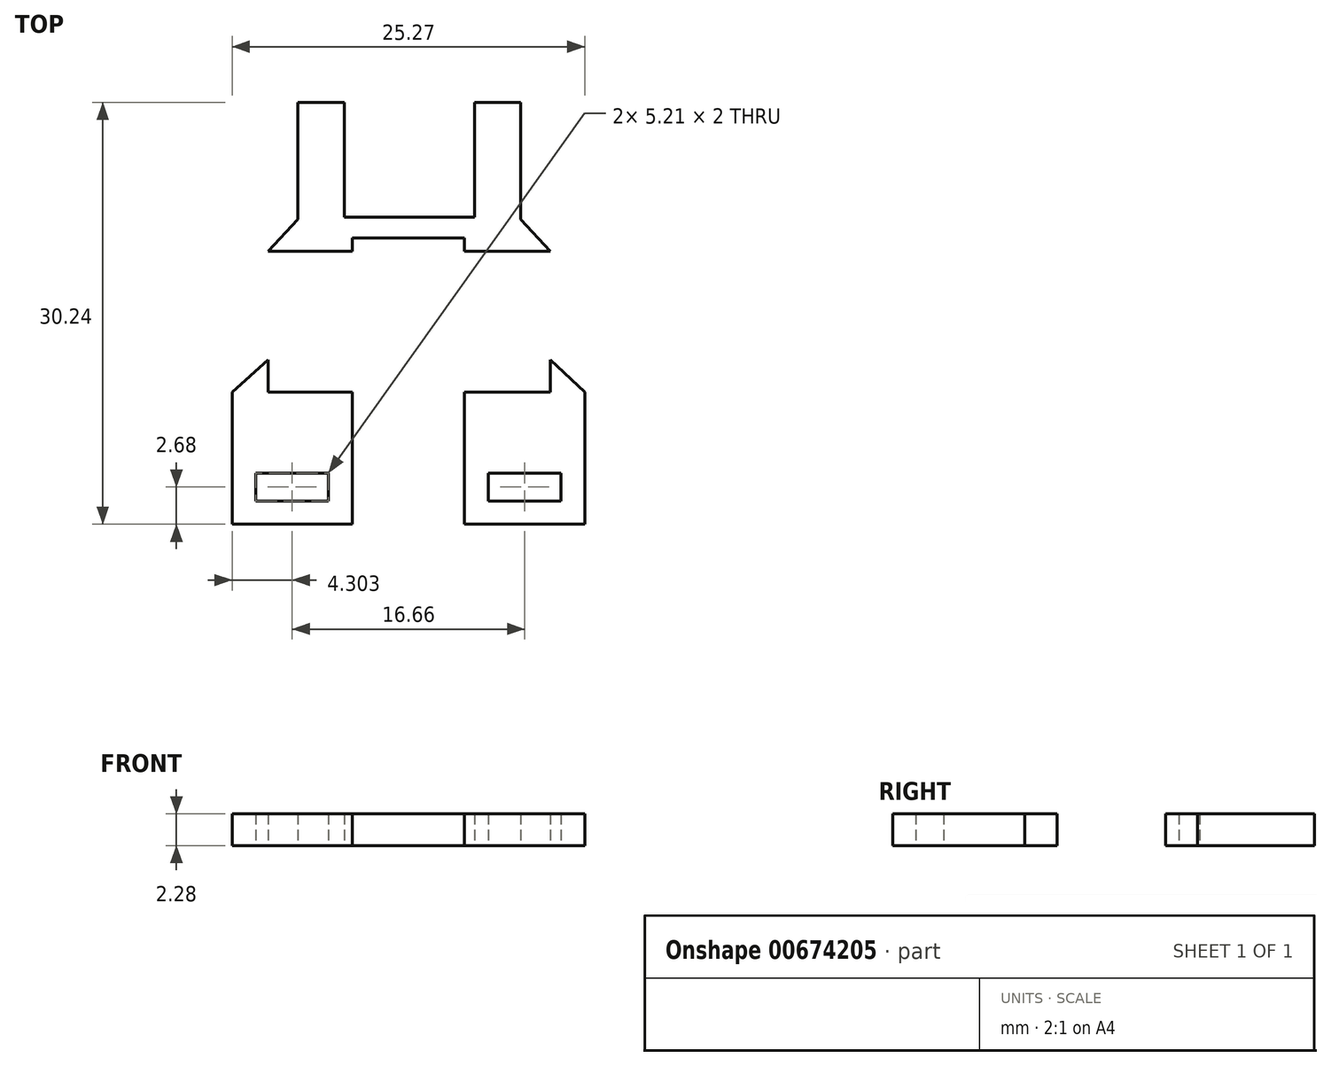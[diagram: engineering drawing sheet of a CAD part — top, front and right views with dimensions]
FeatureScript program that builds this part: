
annotation { "Feature Type Name" : "Feature", "Feature Type Description" : "" }
export const myFeature = defineFeature(function(context is Context, id is Id, definition is map)
    precondition{}
    {
        {
            var Q0;
            Q0=qCreatedBy(makeId("Top.planeOp"),FACE);
            var sketch = newSketch(context, id + "F0", { "sketchPlane" : qUnion([Q0])});
            skLineSegment(sketch, "E0.bottom", {"start": v(-2.7, 0) * mm, "end": v(6.6, 0) * mm});
            skLineSegment(sketch, "E0.top", {"start": v(-2.7, 8.22) * mm, "end": v(6.6, 8.22) * mm});
            skLineSegment(sketch, "E0.left", {"start": v(-2.7, 0) * mm, "end": v(-2.7, 8.22) * mm});
            skLineSegment(sketch, "E0.right", {"start": v(6.6, 0) * mm, "end": v(6.6, 8.22) * mm});
            skLineSegment(sketch, "E1.bottom", {"start": v(-6.03, 8.22) * mm, "end": v(9.94, 8.22) * mm});
            skLineSegment(sketch, "E1.top", {"start": v(-6.03, -2.45) * mm, "end": v(9.94, -2.45) * mm});
            skLineSegment(sketch, "E1.left", {"start": v(-6.03, 8.22) * mm, "end": v(-6.03, -2.45) * mm});
            skLineSegment(sketch, "E1.right", {"start": v(9.94, 8.22) * mm, "end": v(9.94, -2.45) * mm});
            skLineSegment(sketch, "E2.bottom", {"start": v(-8.19, -2.45) * mm, "end": v(12.05, -2.45) * mm});
            skLineSegment(sketch, "E2.top", {"start": v(-8.19, -12.54) * mm, "end": v(12.05, -12.54) * mm});
            skLineSegment(sketch, "E2.left", {"start": v(-8.19, -2.45) * mm, "end": v(-8.19, -12.54) * mm});
            skLineSegment(sketch, "E2.right", {"start": v(12.05, -2.45) * mm, "end": v(12.05, -12.54) * mm});
            skLineSegment(sketch, "E3.bottom", {"start": v(-10.75, -12.54) * mm, "end": v(14.52, -12.54) * mm});
            skLineSegment(sketch, "E3.top", {"start": v(-10.75, -22.02) * mm, "end": v(14.52, -22.02) * mm});
            skLineSegment(sketch, "E3.left", {"start": v(-10.75, -12.54) * mm, "end": v(-10.75, -22.02) * mm});
            skLineSegment(sketch, "E3.right", {"start": v(14.52, -12.54) * mm, "end": v(14.52, -22.02) * mm});
            skLineSegment(sketch, "E4.bottom", {"start": v(-2.14, -22.02) * mm, "end": v(5.9, -22.02) * mm});
            skLineSegment(sketch, "E4.top", {"start": v(-2.14, -1.51) * mm, "end": v(5.9, -1.51) * mm});
            skLineSegment(sketch, "E4.left", {"start": v(-2.14, -22.02) * mm, "end": v(-2.14, -1.51) * mm});
            skLineSegment(sketch, "E4.right", {"start": v(5.9, -22.02) * mm, "end": v(5.9, -1.5) * mm});
            skLineSegment(sketch, "E5", {"start": v(-10.75, -12.54) * mm, "end": v(-8.19, -10.24) * mm});
            skLineSegment(sketch, "E6", {"start": v(-8.19, -2.45) * mm, "end": v(-6.03, -0.15) * mm});
            skLineSegment(sketch, "E7", {"start": v(12.05, -2.45) * mm, "end": v(9.94, -0.15) * mm});
            skLineSegment(sketch, "E8", {"start": v(14.52, -12.54) * mm, "end": v(12.05, -10.24) * mm});
            skLineSegment(sketch, "E9.bottom", {"start": v(-9.05, -18.34) * mm, "end": v(-3.84, -18.34) * mm});
            skLineSegment(sketch, "E9.top", {"start": v(-9.05, -20.34) * mm, "end": v(-3.84, -20.34) * mm});
            skLineSegment(sketch, "E9.left", {"start": v(-9.05, -18.34) * mm, "end": v(-9.05, -20.34) * mm});
            skLineSegment(sketch, "E9.right", {"start": v(-3.84, -18.34) * mm, "end": v(-3.84, -20.34) * mm});
            skLineSegment(sketch, "E10.bottom", {"start": v(7.6, -18.34) * mm, "end": v(12.82, -18.34) * mm});
            skLineSegment(sketch, "E10.top", {"start": v(7.6, -20.34) * mm, "end": v(12.82, -20.34) * mm});
            skLineSegment(sketch, "E10.left", {"start": v(7.6, -18.34) * mm, "end": v(7.6, -20.34) * mm});
            skLineSegment(sketch, "E10.right", {"start": v(12.82, -18.34) * mm, "end": v(12.82, -20.34) * mm});
            skSolve(sketch);
        }
        {
            var Q0;
            {var subQ0=sQuery(id+"F0.wireOp",EDGE,"E3.right");Q0=makeQuery(id+"F0.imprint","IMPRINT",FACE,{"disambiguationData":[TD([[makeQuery(id+"F0.imprint","IMPRINT",EDGE,{"derivedFrom":subQ0}),-1.0]])]});}
            var Q1;
            {var subQ0=sQuery(id+"F0.wireOp",EDGE,"E3.left");Q1=makeQuery(id+"F0.imprint","IMPRINT",FACE,{"disambiguationData":[TD([[makeQuery(id+"F0.imprint","IMPRINT",EDGE,{"derivedFrom":subQ0}),1.0]])]});}
            var Q2;
            {var subQ3=sQuery(id+"F0.wireOp",EDGE,"E5");Q2=makeQuery(id+"F0.imprint","IMPRINT",FACE,{"disambiguationData":[TD([[makeQuery(id+"F0.imprint","IMPRINT",EDGE,{"derivedFrom":subQ3}),-1.0]])]});}
            var Q3;
            {var subQ4=sQuery(id+"F0.wireOp",EDGE,"E2.bottom");var subQ5=makeQuery(id+"F0.imprint","INTERSECT",VERTEX,{"derivedFrom":[sQuery(id+"F0.wireOp",EDGE,"E1.left"),subQ4]});Q3=makeQuery(id+"F0.imprint","IMPRINT",FACE,{"disambiguationData":[TD([[makeQuery(id+"F0.imprint","IMPRINT",EDGE,{"disambiguationData":[TD([[subQ5,-1.0]])],"derivedFrom":subQ4}),-1.0]])]});}
            var Q4;
            {var subQ3=sQuery(id+"F0.wireOp",EDGE,"E6");Q4=makeQuery(id+"F0.imprint","IMPRINT",FACE,{"disambiguationData":[TD([[makeQuery(id+"F0.imprint","IMPRINT",EDGE,{"derivedFrom":subQ3}),-1.0]])]});}
            var Q5;
            Q5=makeQuery(id+"F0.imprint","IMPRINT",FACE,{"disambiguationData":[TD([[makeQuery(id+"F0.imprint","IMPRINT",EDGE,{"derivedFrom":sQuery(id+"F0.wireOp",EDGE,"E0.bottom")}),-1.0]])]});
            var Q6;
            {var subQ1=sQuery(id+"F0.wireOp",EDGE,"E2.bottom");var subQ4=makeQuery(id+"F0.imprint","INTERSECT",VERTEX,{"derivedFrom":[sQuery(id+"F0.wireOp",EDGE,"E1.right"),subQ1]});Q6=makeQuery(id+"F0.imprint","IMPRINT",FACE,{"disambiguationData":[TD([[makeQuery(id+"F0.imprint","IMPRINT",EDGE,{"disambiguationData":[TD([[subQ4,1.0]])],"derivedFrom":subQ1}),-1.0]])]});}
            var Q7;
            {var subQ3=sQuery(id+"F0.wireOp",EDGE,"E7");Q7=makeQuery(id+"F0.imprint","IMPRINT",FACE,{"disambiguationData":[TD([[makeQuery(id+"F0.imprint","IMPRINT",EDGE,{"derivedFrom":subQ3}),1.0]])]});}
            var Q8;
            {var subQ3=sQuery(id+"F0.wireOp",EDGE,"E8");Q8=makeQuery(id+"F0.imprint","IMPRINT",FACE,{"disambiguationData":[TD([[makeQuery(id+"F0.imprint","IMPRINT",EDGE,{"derivedFrom":subQ3}),1.0]])]});}
            extrude(context, id + "F1", {"entities" : qUnion([Q0, Q1, Q2, Q3, Q4, Q5, Q6, Q7, Q8]), "depth" : 2.28 * mm, "offsetDistance" : 25.4 * mm});
        }
    });
